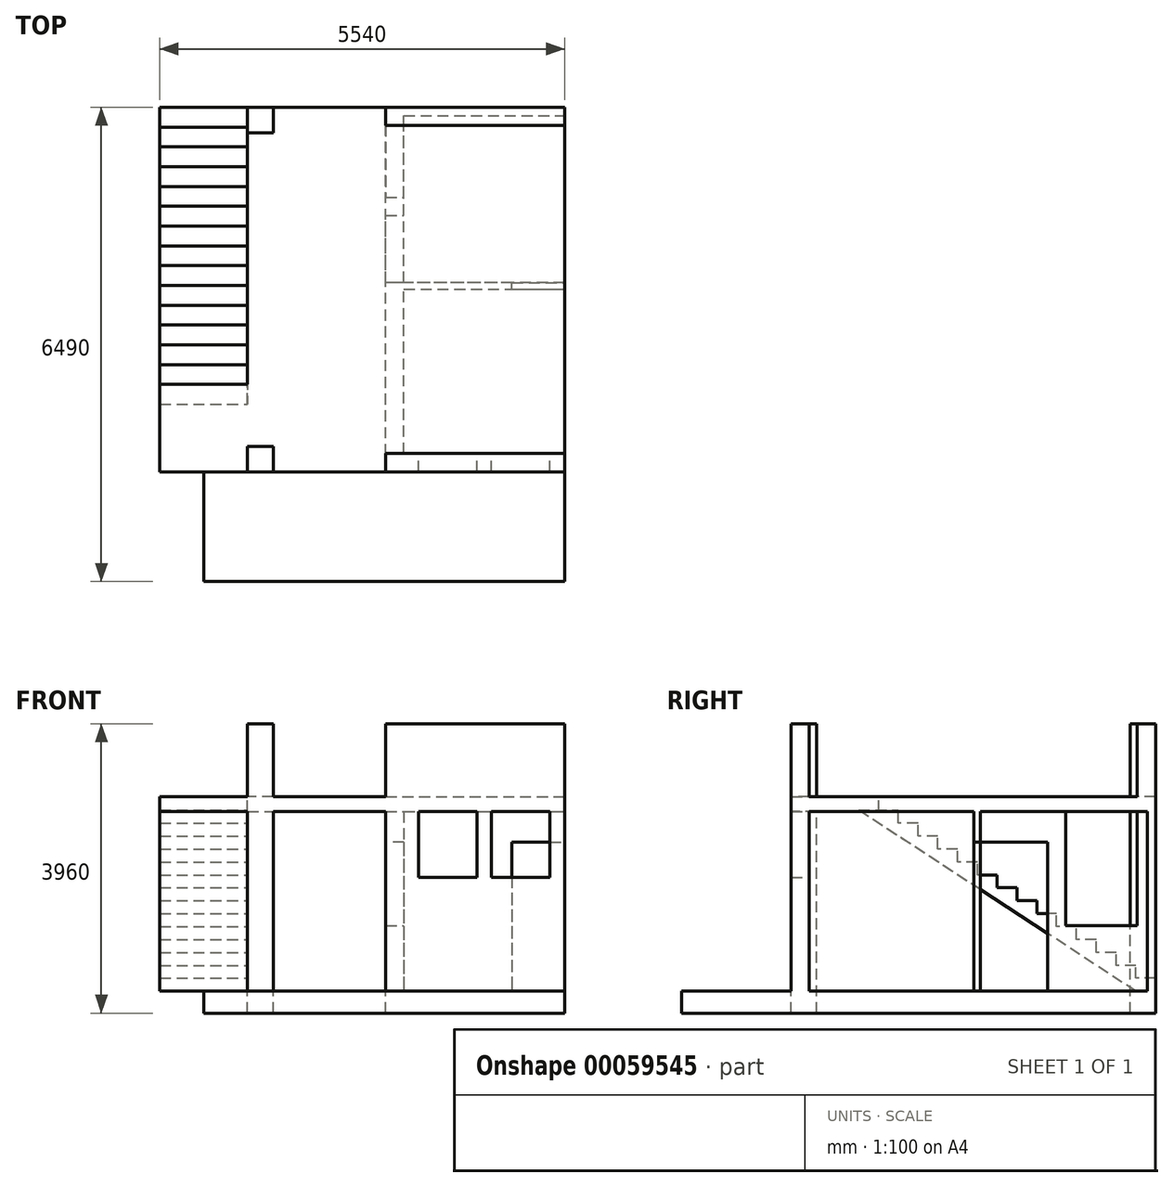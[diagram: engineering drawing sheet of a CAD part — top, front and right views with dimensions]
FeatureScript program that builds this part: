
annotation { "Feature Type Name" : "Feature", "Feature Type Description" : "" }
export const myFeature = defineFeature(function(context is Context, id is Id, definition is map)
    precondition{}
    {
        {
            var Q0;
            Q0=qCreatedBy(makeId("Top.planeOp"),FACE);
            cPlane(context, id + "F0", {"entities" : qUnion([Q0]), "cplaneType" : CPlaneType.OFFSET, "offset" : 2660 * mm, "width" : 150 * mm, "height" : 150 * mm});
        }
        {
            var Q0;
            Q0=qCreatedBy(id+"F0.planeOp",FACE);
            cPlane(context, id + "F1", {"entities" : qUnion([Q0]), "cplaneType" : CPlaneType.OFFSET, "offset" : 1000 * mm, "width" : 150 * mm, "height" : 150 * mm});
        }
        {
            var Q0;
            Q0=qCreatedBy(makeId("Top.planeOp"),FACE);
            var sketch = newSketch(context, id + "F2", { "sketchPlane" : qUnion([Q0])});
            skLineSegment(sketch, "E0.bottom", {"start": v(-5540, 4990) * mm, "end": v(0, 4990) * mm});
            skLineSegment(sketch, "E0.top", {"start": v(-4940, 0) * mm, "end": v(-4340, 0) * mm});
            skLineSegment(sketch, "E0.left", {"start": v(-5540, 4990) * mm, "end": v(-5540, 2590) * mm});
            skLineSegment(sketch, "E0.right", {"start": v(0, 4990) * mm, "end": v(0, 0) * mm});
            skLineSegment(sketch, "E1", {"start": v(-4940, 0) * mm, "end": v(-4940, -1500) * mm});
            skLineSegment(sketch, "E2", {"start": v(-4940, -1500) * mm, "end": v(0, -1500) * mm});
            skLineSegment(sketch, "E3", {"start": v(0, -1500) * mm, "end": v(0, 0) * mm});
            skLineSegment(sketch, "E4", {"start": v(-4340, 0) * mm, "end": v(-4340, 4990) * mm, "construction": true});
            skLineSegment(sketch, "E5", {"start": v(-4340, 4640) * mm, "end": v(-3990, 4640) * mm});
            skLineSegment(sketch, "E6", {"start": v(-3990, 4640) * mm, "end": v(-3990, 4990) * mm});
            skLineSegment(sketch, "E7", {"start": v(-4340, 4640) * mm, "end": v(-4340, 4990) * mm});
            skLineSegment(sketch, "E8", {"start": v(-4340, 0) * mm, "end": v(-4340, 350) * mm});
            skLineSegment(sketch, "E9", {"start": v(-4340, 350) * mm, "end": v(-3990, 350) * mm});
            skLineSegment(sketch, "E10", {"start": v(-3990, 350) * mm, "end": v(-3990, 0) * mm});
            skLineSegment(sketch, "E11", {"start": v(0, 250) * mm, "end": v(-2200, 250) * mm});
            skLineSegment(sketch, "E12", {"start": v(-2200, 0) * mm, "end": v(-2200, 250) * mm, "construction": true});
            skLineSegment(sketch, "E13", {"start": v(-2200, 250) * mm, "end": v(-2200, 2500) * mm});
            skLineSegment(sketch, "E14", {"start": v(-720, 2500) * mm, "end": v(0, 2500) * mm});
            skLineSegment(sketch, "E15", {"start": v(-2200, 2500) * mm, "end": v(-720, 2500) * mm});
            skLineSegment(sketch, "E16", {"start": v(-2200, 250) * mm, "end": v(-2450, 250) * mm});
            skLineSegment(sketch, "E17", {"start": v(-2450, 250) * mm, "end": v(-2450, 0) * mm});
            skLineSegment(sketch, "E18", {"start": v(-2450, 250) * mm, "end": v(-2450, 4990) * mm});
            skLineSegment(sketch, "E19", {"start": v(-720, 2500) * mm, "end": v(-720, 2590) * mm});
            skLineSegment(sketch, "E20", {"start": v(-720, 2590) * mm, "end": v(-2450, 2590) * mm});
            skLineSegment(sketch, "E21", {"start": v(-1229.64, 4990) * mm, "end": v(-1229.64, 4875) * mm, "construction": true});
            skLineSegment(sketch, "E22", {"start": v(-1229.64, 4875) * mm, "end": v(0, 4875) * mm});
            skLineSegment(sketch, "E23", {"start": v(-2200, 2500) * mm, "end": v(-2200, 2590) * mm});
            skLineSegment(sketch, "E24", {"start": v(-2200, 4875) * mm, "end": v(-1229.64, 4875) * mm});
            skLineSegment(sketch, "E25", {"start": v(-3990, 4815) * mm, "end": v(-4165, 4815) * mm, "construction": true});
            skPoint(sketch, "E25.endSnap0", {"position": v(-4165, 4640) * mm});
            skLineSegment(sketch, "E26", {"start": v(-4165, 4815) * mm, "end": v(-4165, 4640) * mm, "construction": true});
            skLineSegment(sketch, "E27", {"start": v(-3990, 4815) * mm, "end": v(-2450, 4815) * mm, "construction": true});
            skLineSegment(sketch, "E28", {"start": v(-2450, 4815) * mm, "end": v(-2200, 4815) * mm, "construction": true});
            skLineSegment(sketch, "E29", {"start": v(-3990, 175) * mm, "end": v(-4165, 175) * mm, "construction": true});
            skPoint(sketch, "E29.endSnap0", {"position": v(-4165, 350) * mm});
            skLineSegment(sketch, "E30", {"start": v(-4165, 175) * mm, "end": v(-4165, 350) * mm, "construction": true});
            skLineSegment(sketch, "E31", {"start": v(-3990, 175) * mm, "end": v(-2450, 175) * mm, "construction": true});
            skLineSegment(sketch, "E32", {"start": v(-4165, 175) * mm, "end": v(-4340, 175) * mm, "construction": true});
            skLineSegment(sketch, "E33", {"start": v(-2200, 4875) * mm, "end": v(-2450, 4875) * mm});
            skLineSegment(sketch, "E34", {"start": v(0, 4740) * mm, "end": v(-2450, 4740) * mm});
            skLineSegment(sketch, "E35", {"start": v(-1793.69, 4990) * mm, "end": v(-1793.69, 4740) * mm, "construction": true});
            skLineSegment(sketch, "E36", {"start": v(-720, 2590) * mm, "end": v(0, 2590) * mm});
            skLineSegment(sketch, "E37", {"start": v(-2450, 3510) * mm, "end": v(-2200, 3510) * mm});
            skLineSegment(sketch, "E38", {"start": v(-2200, 2590) * mm, "end": v(-2200, 3510) * mm});
            skLineSegment(sketch, "E39", {"start": v(-2200, 3510) * mm, "end": v(-2200, 4875) * mm});
            skLineSegment(sketch, "E40", {"start": v(-4340, 2590) * mm, "end": v(-5540, 2590) * mm, "construction": true});
            skLineSegment(sketch, "E41", {"start": v(-4340, 0) * mm, "end": v(0, 0) * mm});
            skLineSegment(sketch, "E42", {"start": v(-5540, 2590) * mm, "end": v(-4940, 0) * mm});
            skLineSegment(sketch, "E43", {"start": v(-5540, 0) * mm, "end": v(-4940, 0) * mm, "construction": true});
            skLineSegment(sketch, "E44", {"start": v(-5540, 0) * mm, "end": v(-5540, 1200) * mm, "construction": true});
            skLineSegment(sketch, "E45", {"start": v(-5540, 1200) * mm, "end": v(-4340, 1200) * mm, "construction": true});
            skLineSegment(sketch, "E46", {"start": v(-5540, 1200) * mm, "end": v(-5540, 2590) * mm, "construction": true});
            skSolve(sketch);
        }
        {
            var Q0;
            {var subQ2=sQuery(id+"F2.wireOp",EDGE,"ok32suX9-RW7e-SiFE-Vpjj-8JhxnI1UVV4A");Q0=makeQuery(id+"F2.imprint","IMPRINT",FACE,{"disambiguationData":[TD([[makeQuery(id+"F2.imprint","IMPRINT",EDGE,{"derivedFrom":subQ2}),-1.0]])]});}
            var Q1;
            Q1=makeQuery(id+"F2.imprint","IMPRINT",FACE,{"disambiguationData":[TD([[makeQuery(id+"F2.imprint","IMPRINT",EDGE,{"derivedFrom":sQuery(id+"F2.wireOp",EDGE,"E5")}),-1.0]])]});
            var Q2;
            {var subQ0=sQuery(id+"F2.wireOp",EDGE,"E15");Q2=makeQuery(id+"F2.imprint","IMPRINT",FACE,{"disambiguationData":[TD([[makeQuery(id+"F2.imprint","IMPRINT",EDGE,{"derivedFrom":subQ0}),1.0]])]});}
            var Q3;
            {var subQ0=sQuery(id+"F2.wireOp",EDGE,"E1");Q3=makeQuery(id+"F2.imprint","IMPRINT",FACE,{"disambiguationData":[TD([[makeQuery(id+"F2.imprint","IMPRINT",EDGE,{"derivedFrom":subQ0}),1.0]])]});}
            var Q4;
            {var subQ8=sQuery(id+"F2.wireOp",EDGE,"E22");Q4=makeQuery(id+"F2.imprint","IMPRINT",FACE,{"disambiguationData":[TD([[makeQuery(id+"F2.imprint","IMPRINT",EDGE,{"derivedFrom":subQ8}),1.0]])]});}
            var Q5;
            Q5=makeQuery(id+"F2.imprint","IMPRINT",FACE,{"disambiguationData":[TD([[makeQuery(id+"F2.imprint","IMPRINT",EDGE,{"derivedFrom":sQuery(id+"F2.wireOp",EDGE,"E5")}),1.0]])]});
            var Q6;
            {var subQ4=sQuery(id+"F2.wireOp",EDGE,"E9");Q6=makeQuery(id+"F2.imprint","IMPRINT",FACE,{"disambiguationData":[TD([[makeQuery(id+"F2.imprint","IMPRINT",EDGE,{"derivedFrom":subQ4}),-1.0]])]});}
            var Q7;
            {var subQ4=sQuery(id+"F2.wireOp",EDGE,"E11");Q7=makeQuery(id+"F2.imprint","IMPRINT",FACE,{"disambiguationData":[TD([[makeQuery(id+"F2.imprint","IMPRINT",EDGE,{"derivedFrom":subQ4}),-1.0]])]});}
            var Q8;
            {var subQ3=sQuery(id+"F2.wireOp",EDGE,"E11");Q8=makeQuery(id+"F2.imprint","IMPRINT",FACE,{"disambiguationData":[TD([[makeQuery(id+"F2.imprint","IMPRINT",EDGE,{"derivedFrom":subQ3}),1.0]])]});}
            var Q9;
            {var subQ0=sQuery(id+"F2.wireOp",EDGE,"E20");var subQ1=sQuery(id+"F2.wireOp",EDGE,"E18");var subQ2=makeQuery(id+"F2.imprint","INTERSECT",VERTEX,{"derivedFrom":[subQ1,subQ0]});Q9=makeQuery(id+"F2.imprint","IMPRINT",FACE,{"disambiguationData":[TD([[makeQuery(id+"F2.imprint","IMPRINT",EDGE,{"disambiguationData":[TD([[subQ2,-1.0]])],"derivedFrom":subQ1}),-1.0]])]});}
            var Q10;
            {var subQ4=sQuery(id+"F2.wireOp",EDGE,"E22");Q10=makeQuery(id+"F2.imprint","IMPRINT",FACE,{"disambiguationData":[TD([[makeQuery(id+"F2.imprint","IMPRINT",EDGE,{"derivedFrom":subQ4}),-1.0]])]});}
            var Q11;
            {var subQ0=sQuery(id+"F2.wireOp",EDGE,"E33");Q11=makeQuery(id+"F2.imprint","IMPRINT",FACE,{"disambiguationData":[TD([[makeQuery(id+"F2.imprint","IMPRINT",EDGE,{"derivedFrom":subQ0}),1.0]])]});}
            var Q12;
            {var subQ6=sQuery(id+"F2.wireOp",EDGE,"E13");Q12=makeQuery(id+"F2.imprint","IMPRINT",FACE,{"disambiguationData":[TD([[makeQuery(id+"F2.imprint","IMPRINT",EDGE,{"derivedFrom":subQ6}),1.0]])]});}
            var Q13;
            {var subQ3=sQuery(id+"F2.wireOp",EDGE,"E37");Q13=makeQuery(id+"F2.imprint","IMPRINT",FACE,{"disambiguationData":[TD([[makeQuery(id+"F2.imprint","IMPRINT",EDGE,{"derivedFrom":subQ3}),1.0]])]});}
            var Q14;
            {var subQ0=sQuery(id+"F2.wireOp",EDGE,"E36");Q14=makeQuery(id+"F2.imprint","IMPRINT",FACE,{"disambiguationData":[TD([[makeQuery(id+"F2.imprint","IMPRINT",EDGE,{"derivedFrom":subQ0}),1.0]])]});}
            var Q15;
            {var subQ0=sQuery(id+"F2.wireOp",EDGE,"E14");Q15=makeQuery(id+"F2.imprint","IMPRINT",FACE,{"disambiguationData":[TD([[makeQuery(id+"F2.imprint","IMPRINT",EDGE,{"derivedFrom":subQ0}),1.0]])]});}
            extrude(context, id + "F3", {"entities" : qUnion([Q0, Q1, Q2, Q3, Q4, Q5, Q6, Q7, Q8, Q9, Q10, Q11, Q12, Q13, Q14, Q15]), "oppositeDirection" : true, "depth" : 300 * mm});
        }
        {
            var Q0;
            Q0=qCreatedBy(id+"F0.planeOp",FACE);
            var sketch = newSketch(context, id + "F4", { "sketchPlane" : qUnion([Q0])});
            skLineSegment(sketch, "E47", {"start": v(-5540, 1200) * mm, "end": v(-5540, 0) * mm});
            skLineSegment(sketch, "E48", {"start": v(-5540, 0) * mm, "end": v(-4340, 0) * mm});
            skLineSegment(sketch, "E49", {"start": v(-4340, 0) * mm, "end": v(-4340, 175) * mm});
            skLineSegment(sketch, "E50", {"start": v(-4340, 175) * mm, "end": v(-3990, 175) * mm});
            skLineSegment(sketch, "E51", {"start": v(-3990, 175) * mm, "end": v(-3990, 0) * mm});
            skLineSegment(sketch, "E52", {"start": v(-3990, 0) * mm, "end": v(-2450, 0) * mm});
            skLineSegment(sketch, "E53", {"start": v(-2450, 0) * mm, "end": v(-2450, 175) * mm});
            skLineSegment(sketch, "E54", {"start": v(-2450, 175) * mm, "end": v(0, 175) * mm});
            skLineSegment(sketch, "E55", {"start": v(-5540, 1200) * mm, "end": v(-4340, 1200) * mm});
            skLineSegment(sketch, "E56", {"start": v(-4340, 1200) * mm, "end": v(-4340, 4640) * mm});
            skLineSegment(sketch, "E57", {"start": v(-4340, 4640) * mm, "end": v(-4165, 4640) * mm});
            skLineSegment(sketch, "E58", {"start": v(-4165, 4640) * mm, "end": v(-4165, 4815) * mm});
            skLineSegment(sketch, "E59", {"start": v(-4165, 4815) * mm, "end": v(-3990, 4815) * mm});
            skLineSegment(sketch, "E60", {"start": v(-3990, 4815) * mm, "end": v(-3990, 4990) * mm});
            skLineSegment(sketch, "E61", {"start": v(-3990, 4990) * mm, "end": v(-2450, 4990) * mm});
            skLineSegment(sketch, "E62", {"start": v(-2450, 4990) * mm, "end": v(-2450, 4815) * mm});
            skLineSegment(sketch, "E63", {"start": v(-2450, 4815) * mm, "end": v(0, 4815) * mm});
            skLineSegment(sketch, "E64", {"start": v(0, 4815) * mm, "end": v(0, 175) * mm});
            skSolve(sketch);
        }
        {
            var Q0;
            Q0 = qSketchRegion(id + "F4", true);
            extrude(context, id + "F5", {"entities" : qUnion([Q0]), "oppositeDirection" : true, "depth" : 200 * mm});
        }
        {
            var Q0;
            {var subQ0=sQuery(id+"F2.wireOp",EDGE,"E22");Q0=makeQuery(id+"F2.imprint","IMPRINT",FACE,{"disambiguationData":[TD([[makeQuery(id+"F2.imprint","IMPRINT",EDGE,{"derivedFrom":subQ0}),1.0]])]});}
            var Q1;
            {var subQ0=sQuery(id+"F2.wireOp",EDGE,"E33");Q1=makeQuery(id+"F2.imprint","IMPRINT",FACE,{"disambiguationData":[TD([[makeQuery(id+"F2.imprint","IMPRINT",EDGE,{"derivedFrom":subQ0}),1.0]])]});}
            var Q2;
            {var subQ0=sQuery(id+"F2.wireOp",EDGE,"E20");var subQ1=sQuery(id+"F2.wireOp",EDGE,"E18");var subQ2=makeQuery(id+"F2.imprint","INTERSECT",VERTEX,{"derivedFrom":[subQ1,subQ0]});Q2=makeQuery(id+"F2.imprint","IMPRINT",FACE,{"disambiguationData":[TD([[makeQuery(id+"F2.imprint","IMPRINT",EDGE,{"disambiguationData":[TD([[subQ2,-1.0]])],"derivedFrom":subQ1}),-1.0]])]});}
            var Q3;
            {var subQ0=sQuery(id+"F2.wireOp",EDGE,"E15");Q3=makeQuery(id+"F2.imprint","IMPRINT",FACE,{"disambiguationData":[TD([[makeQuery(id+"F2.imprint","IMPRINT",EDGE,{"derivedFrom":subQ0}),1.0]])]});}
            var Q4;
            {var subQ6=sQuery(id+"F2.wireOp",EDGE,"E13");Q4=makeQuery(id+"F2.imprint","IMPRINT",FACE,{"disambiguationData":[TD([[makeQuery(id+"F2.imprint","IMPRINT",EDGE,{"derivedFrom":subQ6}),1.0]])]});}
            var Q5;
            {var subQ3=sQuery(id+"F2.wireOp",EDGE,"E37");Q5=makeQuery(id+"F2.imprint","IMPRINT",FACE,{"disambiguationData":[TD([[makeQuery(id+"F2.imprint","IMPRINT",EDGE,{"derivedFrom":subQ3}),1.0]])]});}
            var Q6;
            {var subQ0=sQuery(id+"F2.wireOp",EDGE,"E14");Q6=makeQuery(id+"F2.imprint","IMPRINT",FACE,{"disambiguationData":[TD([[makeQuery(id+"F2.imprint","IMPRINT",EDGE,{"derivedFrom":subQ0}),1.0]])]});}
            var Q7;
            Q7=makeQuery(id+"F5.opExtrude","CAP_FACE",FACE,{"disambiguationData":[OSD([sQuery(id+"F4.wireOp",EDGE,"E47"),sQuery(id+"F4.wireOp",EDGE,"E48"),sQuery(id+"F4.wireOp",EDGE,"E49"),sQuery(id+"F4.wireOp",EDGE,"E50"),sQuery(id+"F4.wireOp",EDGE,"E51"),sQuery(id+"F4.wireOp",EDGE,"E52"),sQuery(id+"F4.wireOp",EDGE,"E53"),sQuery(id+"F4.wireOp",EDGE,"E54"),sQuery(id+"F4.wireOp",EDGE,"E55"),sQuery(id+"F4.wireOp",EDGE,"E56"),sQuery(id+"F4.wireOp",EDGE,"E57"),sQuery(id+"F4.wireOp",EDGE,"E58"),sQuery(id+"F4.wireOp",EDGE,"E59"),sQuery(id+"F4.wireOp",EDGE,"E60"),sQuery(id+"F4.wireOp",EDGE,"E61"),sQuery(id+"F4.wireOp",EDGE,"E62"),sQuery(id+"F4.wireOp",EDGE,"E63"),sQuery(id+"F4.wireOp",EDGE,"E64")])],"isStart":false});
            extrude(context, id + "F6", {"entities" : qUnion([Q0, Q1, Q2, Q3, Q4, Q5, Q6]), "endBound" : BoundingType.UP_TO_SURFACE, "endBoundEntityFace" : qUnion([Q7]), "depth" : 25 * mm});
        }
        {
            var Q0;
            {var subQ4=sQuery(id+"F2.wireOp",EDGE,"E22");Q0=makeQuery(id+"F2.imprint","IMPRINT",FACE,{"disambiguationData":[TD([[makeQuery(id+"F2.imprint","IMPRINT",EDGE,{"derivedFrom":subQ4}),-1.0]])]});}
            var Q1;
            {var subQ0=sQuery(id+"F2.wireOp",EDGE,"E22");Q1=makeQuery(id+"F2.imprint","IMPRINT",FACE,{"disambiguationData":[TD([[makeQuery(id+"F2.imprint","IMPRINT",EDGE,{"derivedFrom":subQ0}),1.0]])]});}
            var Q2;
            {var subQ0=sQuery(id+"F2.wireOp",EDGE,"E33");Q2=makeQuery(id+"F2.imprint","IMPRINT",FACE,{"disambiguationData":[TD([[makeQuery(id+"F2.imprint","IMPRINT",EDGE,{"derivedFrom":subQ0}),1.0]])]});}
            var Q3;
            Q3=qCreatedBy(id+"F1.planeOp",FACE);
            var Q4;
            Q4=makeQuery(id+"F5.opExtrude","CAP_FACE",FACE,{"disambiguationData":[OSD([sQuery(id+"F4.wireOp",EDGE,"E47"),sQuery(id+"F4.wireOp",EDGE,"E48"),sQuery(id+"F4.wireOp",EDGE,"E49"),sQuery(id+"F4.wireOp",EDGE,"E50"),sQuery(id+"F4.wireOp",EDGE,"E51"),sQuery(id+"F4.wireOp",EDGE,"E52"),sQuery(id+"F4.wireOp",EDGE,"E53"),sQuery(id+"F4.wireOp",EDGE,"E54"),sQuery(id+"F4.wireOp",EDGE,"E55"),sQuery(id+"F4.wireOp",EDGE,"E56"),sQuery(id+"F4.wireOp",EDGE,"E57"),sQuery(id+"F4.wireOp",EDGE,"E58"),sQuery(id+"F4.wireOp",EDGE,"E59"),sQuery(id+"F4.wireOp",EDGE,"E60"),sQuery(id+"F4.wireOp",EDGE,"E61"),sQuery(id+"F4.wireOp",EDGE,"E62"),sQuery(id+"F4.wireOp",EDGE,"E63"),sQuery(id+"F4.wireOp",EDGE,"E64")])],"isStart":false});
            var Q5;
            Q5=makeQuery(id+"F6.opExtrude","SWEPT_BODY",BODY,{"disambiguationData":[OSD([sQuery(id+"F2.wireOp",EDGE,"E0.bottom"),sQuery(id+"F2.wireOp",EDGE,"E0.right"),sQuery(id+"F2.wireOp",EDGE,"E13"),sQuery(id+"F2.wireOp",EDGE,"E15"),sQuery(id+"F2.wireOp",EDGE,"E16"),sQuery(id+"F2.wireOp",EDGE,"E18"),sQuery(id+"F2.wireOp",EDGE,"E19"),sQuery(id+"F2.wireOp",EDGE,"E20"),sQuery(id+"F2.wireOp",EDGE,"E22"),sQuery(id+"F2.wireOp",EDGE,"E23"),sQuery(id+"F2.wireOp",EDGE,"E24")])]});
            extrude(context, id + "F7", {"entities" : qUnion([Q0, Q1, Q2]), "operationType" : NewBodyOperationType.ADD, "endBound" : BoundingType.UP_TO_SURFACE, "endBoundEntityFace" : qUnion([Q3]), "depth" : 25 * mm, "hasSecondDirection" : true, "secondDirectionBound" : BoundingType.UP_TO_SURFACE, "secondDirectionOppositeDirection" : false, "secondDirectionBoundEntityFace" : qUnion([Q4]), "secondDirectionBoundEntityBody" : qUnion([Q5]), "secondDirectionDepth" : 2000 * mm});
        }
        {
            var Q0;
            {var subQ0=sQuery(id+"F2.wireOp",EDGE,"E11");Q0=makeQuery(id+"F2.imprint","IMPRINT",FACE,{"disambiguationData":[TD([[makeQuery(id+"F2.imprint","IMPRINT",EDGE,{"derivedFrom":subQ0}),1.0]])]});}
            var Q1;
            {var subQ4=sQuery(id+"F2.wireOp",EDGE,"E9");Q1=makeQuery(id+"F2.imprint","IMPRINT",FACE,{"disambiguationData":[TD([[makeQuery(id+"F2.imprint","IMPRINT",EDGE,{"derivedFrom":subQ4}),-1.0]])]});}
            var Q2;
            Q2=makeQuery(id+"F2.imprint","IMPRINT",FACE,{"disambiguationData":[TD([[makeQuery(id+"F2.imprint","IMPRINT",EDGE,{"derivedFrom":sQuery(id+"F2.wireOp",EDGE,"E5")}),1.0]])]});
            var Q3;
            Q3=qCreatedBy(id+"F1.planeOp",FACE);
            extrude(context, id + "F8", {"entities" : qUnion([Q0, Q1, Q2]), "operationType" : NewBodyOperationType.ADD, "endBound" : BoundingType.UP_TO_SURFACE, "endBoundEntityFace" : qUnion([Q3]), "depth" : 25 * mm, "hasSecondDirection" : true, "secondDirectionBound" : BoundingType.UP_TO_NEXT, "secondDirectionOppositeDirection" : true, "secondDirectionDepth" : 25 * mm});
        }
        {
            var Q0;
            Q0=makeQuery(id+"F8.opExtrude","SWEPT_FACE",FACE,{"disambiguationData":[OSD([sQuery(id+"F2.wireOp",EDGE,"E7")])]});
            var sketch = newSketch(context, id + "F9", { "sketchPlane" : qUnion([Q0])});
            skLineSegment(sketch, "E65.bottom", {"start": v(-4990, 0) * mm, "end": v(-4719, 0) * mm});
            skLineSegment(sketch, "E65.top", {"start": v(-4990, 177) * mm, "end": v(-4719, 177) * mm});
            skLineSegment(sketch, "E65.left", {"start": v(-4990, 0) * mm, "end": v(-4990, 177) * mm});
            skLineSegment(sketch, "E65.right", {"start": v(-4719, 0) * mm, "end": v(-4719, 177) * mm});
            skLineSegment(sketch, "E66.bottom", {"start": v(-4719, 177) * mm, "end": v(-4448, 177) * mm});
            skLineSegment(sketch, "E66.top", {"start": v(-4719, 354) * mm, "end": v(-4448, 354) * mm});
            skLineSegment(sketch, "E66.left", {"start": v(-4719, 177) * mm, "end": v(-4719, 354) * mm});
            skLineSegment(sketch, "E66.right", {"start": v(-4448, 177) * mm, "end": v(-4448, 354) * mm});
            skLineSegment(sketch, "E67.bottom", {"start": v(-4448, 354) * mm, "end": v(-4177, 354) * mm});
            skLineSegment(sketch, "E67.top", {"start": v(-4448, 531) * mm, "end": v(-4177, 531) * mm});
            skLineSegment(sketch, "E67.left", {"start": v(-4448, 354) * mm, "end": v(-4448, 531) * mm});
            skLineSegment(sketch, "E67.right", {"start": v(-4177, 354) * mm, "end": v(-4177, 531) * mm});
            skLineSegment(sketch, "E68.bottom", {"start": v(-4177, 531) * mm, "end": v(-3906, 531) * mm});
            skLineSegment(sketch, "E68.top", {"start": v(-4177, 708) * mm, "end": v(-3906, 708) * mm});
            skLineSegment(sketch, "E68.left", {"start": v(-4177, 531) * mm, "end": v(-4177, 708) * mm});
            skLineSegment(sketch, "E68.right", {"start": v(-3906, 531) * mm, "end": v(-3906, 708) * mm});
            skLineSegment(sketch, "E69.bottom", {"start": v(-3906, 708) * mm, "end": v(-3635, 708) * mm});
            skLineSegment(sketch, "E69.top", {"start": v(-3906, 885) * mm, "end": v(-3635, 885) * mm});
            skLineSegment(sketch, "E69.left", {"start": v(-3906, 708) * mm, "end": v(-3906, 885) * mm});
            skLineSegment(sketch, "E69.right", {"start": v(-3635, 708) * mm, "end": v(-3635, 885) * mm});
            skLineSegment(sketch, "E70.bottom", {"start": v(-3635, 885) * mm, "end": v(-3364, 885) * mm});
            skLineSegment(sketch, "E70.top", {"start": v(-3635, 1062) * mm, "end": v(-3364, 1062) * mm});
            skLineSegment(sketch, "E70.left", {"start": v(-3635, 885) * mm, "end": v(-3635, 1062) * mm});
            skLineSegment(sketch, "E70.right", {"start": v(-3364, 885) * mm, "end": v(-3364, 1062) * mm});
            skLineSegment(sketch, "E71.bottom", {"start": v(-3364, 1062) * mm, "end": v(-3093, 1062) * mm});
            skLineSegment(sketch, "E71.top", {"start": v(-3364, 1239) * mm, "end": v(-3093, 1239) * mm});
            skLineSegment(sketch, "E71.left", {"start": v(-3364, 1062) * mm, "end": v(-3364, 1239) * mm});
            skLineSegment(sketch, "E71.right", {"start": v(-3093, 1062) * mm, "end": v(-3093, 1239) * mm});
            skLineSegment(sketch, "E72.top", {"start": v(-2551, 1770) * mm, "end": v(-2280, 1770) * mm});
            skLineSegment(sketch, "E73.top", {"start": v(-2822, 1593) * mm, "end": v(-2551, 1593) * mm});
            skLineSegment(sketch, "E73.left", {"start": v(-2822, 1416) * mm, "end": v(-2822, 1593) * mm});
            skLineSegment(sketch, "E73.right", {"start": v(-2551, 1416) * mm, "end": v(-2551, 1593) * mm});
            skLineSegment(sketch, "E74.top", {"start": v(-3093, 1416) * mm, "end": v(-2822, 1416) * mm});
            skLineSegment(sketch, "E74.right", {"start": v(-2822, 1239) * mm, "end": v(-2822, 1416) * mm});
            skLineSegment(sketch, "E73.bottom", {"start": v(-2822, 1416) * mm, "end": v(-2551, 1416) * mm});
            skLineSegment(sketch, "E75.bottom", {"start": v(-2009, 1947) * mm, "end": v(-1738, 1947) * mm});
            skLineSegment(sketch, "E72.left", {"start": v(-2551, 1593) * mm, "end": v(-2551, 1770) * mm});
            skLineSegment(sketch, "E75.top", {"start": v(-2009, 2124) * mm, "end": v(-1738, 2124) * mm});
            skLineSegment(sketch, "E75.left", {"start": v(-2009, 1947) * mm, "end": v(-2009, 2124) * mm});
            skLineSegment(sketch, "E72.right", {"start": v(-2280, 1593) * mm, "end": v(-2280, 1770) * mm});
            skLineSegment(sketch, "E75.right", {"start": v(-1738, 1947) * mm, "end": v(-1738, 2124) * mm});
            skLineSegment(sketch, "E76.bottom", {"start": v(-2280, 1770) * mm, "end": v(-2009, 1770) * mm});
            skLineSegment(sketch, "E76.top", {"start": v(-2280, 1947) * mm, "end": v(-2009, 1947) * mm});
            skLineSegment(sketch, "E76.left", {"start": v(-2280, 1770) * mm, "end": v(-2280, 1947) * mm});
            skLineSegment(sketch, "E72.bottom", {"start": v(-2551, 1593) * mm, "end": v(-2280, 1593) * mm});
            skLineSegment(sketch, "E76.right", {"start": v(-2009, 1770) * mm, "end": v(-2009, 1947) * mm});
            skLineSegment(sketch, "E74.left", {"start": v(-3093, 1239) * mm, "end": v(-3093, 1416) * mm});
            skLineSegment(sketch, "E74.bottom", {"start": v(-3093, 1239) * mm, "end": v(-2822, 1239) * mm});
            skLineSegment(sketch, "E77.bottom", {"start": v(-1738, 2124) * mm, "end": v(-1467, 2124) * mm});
            skLineSegment(sketch, "E77.top", {"start": v(-1738, 2301) * mm, "end": v(-1467, 2301) * mm});
            skLineSegment(sketch, "E77.left", {"start": v(-1738, 2124) * mm, "end": v(-1738, 2301) * mm});
            skLineSegment(sketch, "E77.right", {"start": v(-1467, 2124) * mm, "end": v(-1467, 2301) * mm});
            skLineSegment(sketch, "E78.bottom", {"start": v(-1467, 2301) * mm, "end": v(-1196, 2301) * mm});
            skLineSegment(sketch, "E78.top", {"start": v(-1467, 2478) * mm, "end": v(-1196, 2478) * mm});
            skLineSegment(sketch, "E78.left", {"start": v(-1467, 2301) * mm, "end": v(-1467, 2478) * mm});
            skLineSegment(sketch, "E78.right", {"start": v(-1196, 2301) * mm, "end": v(-1196, 2478) * mm});
            skLineSegment(sketch, "E79", {"start": v(-4719, 0) * mm, "end": v(-4448, 177) * mm});
            skLineSegment(sketch, "E80", {"start": v(-4448, 177) * mm, "end": v(-4177, 354) * mm});
            skLineSegment(sketch, "E81", {"start": v(-4177, 354) * mm, "end": v(-3906, 531) * mm});
            skLineSegment(sketch, "E82", {"start": v(-3906, 531) * mm, "end": v(-3635, 708) * mm});
            skLineSegment(sketch, "E83", {"start": v(-3635, 708) * mm, "end": v(-3364, 885) * mm});
            skLineSegment(sketch, "E84", {"start": v(-3364, 885) * mm, "end": v(-1196, 2301) * mm});
            skLineSegment(sketch, "E85", {"start": v(-1196, 2301) * mm, "end": v(-925, 2478) * mm});
            skLineSegment(sketch, "E86", {"start": v(-925, 2478) * mm, "end": v(-1196, 2478) * mm});
            skSolve(sketch);
        }
        {
            var Q0;
            Q0 = qSketchRegion(id + "F9", true);
            extrude(context, id + "F10", {"entities" : qUnion([Q0]), "depth" : 1200 * mm});
        }
        {
            var Q0;
            {var subQ3=sQuery(id+"F2.wireOp",EDGE,"E37");Q0=makeQuery(id+"F2.imprint","IMPRINT",FACE,{"disambiguationData":[TD([[makeQuery(id+"F2.imprint","IMPRINT",EDGE,{"derivedFrom":subQ3}),-1.0]])]});}
            var Q1;
            {var subQ0=sQuery(id+"F2.wireOp",EDGE,"E14");Q1=makeQuery(id+"F2.imprint","IMPRINT",FACE,{"disambiguationData":[TD([[makeQuery(id+"F2.imprint","IMPRINT",EDGE,{"derivedFrom":subQ0}),1.0]])]});}
            extrude(context, id + "F11", {"entities" : qUnion([Q0, Q1]), "operationType" : NewBodyOperationType.REMOVE, "depth" : 2040 * mm});
        }
        {
            var Q0;
            Q0=makeQuery(id+"F8.opExtrude","SWEPT_FACE",FACE,{"disambiguationData":[OSD([sQuery(id+"F2.wireOp",EDGE,"E11"),sQuery(id+"F2.wireOp",EDGE,"E16")])]});
            var sketch = newSketch(context, id + "F12", { "sketchPlane" : qUnion([Q0])});
            skLineSegment(sketch, "E87.bottom", {"start": v(200, 2460) * mm, "end": v(1000, 2460) * mm});
            skLineSegment(sketch, "E87.top", {"start": v(200, 1560) * mm, "end": v(1000, 1560) * mm});
            skLineSegment(sketch, "E87.left", {"start": v(200, 2460) * mm, "end": v(200, 1560) * mm});
            skLineSegment(sketch, "E87.right", {"start": v(1000, 2460) * mm, "end": v(1000, 1560) * mm});
            skLineSegment(sketch, "E88.bottom", {"start": v(1200, 2460) * mm, "end": v(2000, 2460) * mm});
            skLineSegment(sketch, "E88.top", {"start": v(1200, 1560) * mm, "end": v(2000, 1560) * mm});
            skLineSegment(sketch, "E88.left", {"start": v(1200, 2460) * mm, "end": v(1200, 1560) * mm});
            skLineSegment(sketch, "E88.right", {"start": v(2000, 2460) * mm, "end": v(2000, 1560) * mm});
            skLineSegment(sketch, "E89", {"start": v(200, 2460) * mm, "end": v(0, 2460) * mm});
            skLineSegment(sketch, "E90", {"start": v(1000, 2460) * mm, "end": v(1200, 2460) * mm});
            skLineSegment(sketch, "E91", {"start": v(2000, 2460) * mm, "end": v(2200, 2460) * mm});
            skSolve(sketch);
        }
        {
            var Q0;
            Q0=makeQuery(id+"F12.imprint","IMPRINT",FACE,{"disambiguationData":[TD([[makeQuery(id+"F12.imprint","IMPRINT",EDGE,{"derivedFrom":sQuery(id+"F12.wireOp",EDGE,"E87.bottom")}),-1.0]])]});
            var Q1;
            Q1=makeQuery(id+"F12.imprint","IMPRINT",FACE,{"disambiguationData":[TD([[makeQuery(id+"F12.imprint","IMPRINT",EDGE,{"derivedFrom":sQuery(id+"F12.wireOp",EDGE,"E88.bottom")}),-1.0]])]});
            var Q2;
            {var subQ0=sQuery(id+"F2.wireOp",EDGE,"E41");Q2=makeQuery(id+"F8.opExtrude","SWEPT_FACE",FACE,{"disambiguationData":[OSD([subQ0]),TDD([makeQuery(id+"F2.imprint","IMPRINT",EDGE,{"disambiguationData":[TD([[makeQuery(id+"F2.imprint","INTERSECT",VERTEX,{"derivedFrom":[sQuery(id+"F2.wireOp",EDGE,"E17"),subQ0]}),-1.0]])],"derivedFrom":subQ0})])]});}
            extrude(context, id + "F13", {"entities" : qUnion([Q0, Q1]), "operationType" : NewBodyOperationType.REMOVE, "endBound" : BoundingType.UP_TO_SURFACE, "oppositeDirection" : true, "endBoundEntityFace" : qUnion([Q2]), "depth" : 25 * mm});
        }
        {
            var Q0;
            Q0=makeQuery(id+"F6.opExtrude","SWEPT_FACE",FACE,{"disambiguationData":[OSD([sQuery(id+"F2.wireOp",EDGE,"E38"),sQuery(id+"F2.wireOp",EDGE,"E39")])]});
            var sketch = newSketch(context, id + "F14", { "sketchPlane" : qUnion([Q0])});
            skLineSegment(sketch, "E92.bottom", {"start": v(3760, 2460) * mm, "end": v(4740, 2460) * mm});
            skLineSegment(sketch, "E92.top", {"start": v(3760, 900) * mm, "end": v(4740, 900) * mm});
            skLineSegment(sketch, "E92.left", {"start": v(3760, 2460) * mm, "end": v(3760, 900) * mm});
            skLineSegment(sketch, "E92.right", {"start": v(4740, 2460) * mm, "end": v(4740, 900) * mm});
            skLineSegment(sketch, "E93", {"start": v(3760, 900) * mm, "end": v(3760, 0) * mm, "construction": true});
            skLineSegment(sketch, "E94", {"start": v(3760, 900) * mm, "end": v(3510, 900) * mm});
            skSolve(sketch);
        }
        {
            var Q0;
            Q0 = qSketchRegion(id + "F14", true);
            extrude(context, id + "F15", {"entities" : qUnion([Q0]), "operationType" : NewBodyOperationType.REMOVE, "endBound" : BoundingType.UP_TO_NEXT, "oppositeDirection" : true, "depth" : 25 * mm});
        }
    });
